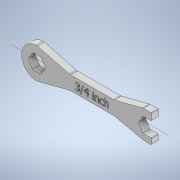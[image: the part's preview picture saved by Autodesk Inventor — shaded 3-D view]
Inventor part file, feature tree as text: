
AUTODESK INVENTOR PART (.ipt)
format: ipt  version: 2020.2 (Build 242310000, 310)  size: 449,536 bytes
history: native  units: in
note: dims shown in document units (in); Inventor stores cm internally (conversion verified against a paired STEP export)
features: extrude x3, sketch x3, fillet x2
ambient origin geometry x8: Origin, YZ Plane, XZ Plane, XY Plane, X Axis, Y Axis, Z Axis, Center Point
bodies: Body1 (feature_tree)
feature tree (8):
  extrude  "Extrusion2"  Depth=0.375in
  fillet  "Fillet1"  Radius=0.375in
  fillet  "Fillet2"  Radius=0.375in
  extrude  "Extrusion3"  Depth=0.0312in
  extrude  "Extrusion4"  TaperAngle=0.0deg  [1 undecoded]
  sketch  "Sketch2"  dims[d23=0.375in d24=0.375in d26=0.375in d27=0.375in]
  sketch  "Sketch3"  dims[d28=0.0in d29=0.0312in]
  sketch  "Sketch6"  dims[d30=0.25in d32=0.0in d33=0.125in d34=0.0in]
note: 1 required parameter value undecoded (feature->parameter linkage not recoverable at this tier; creation-order binding heuristic only, values carry confidence <= 0.55)
